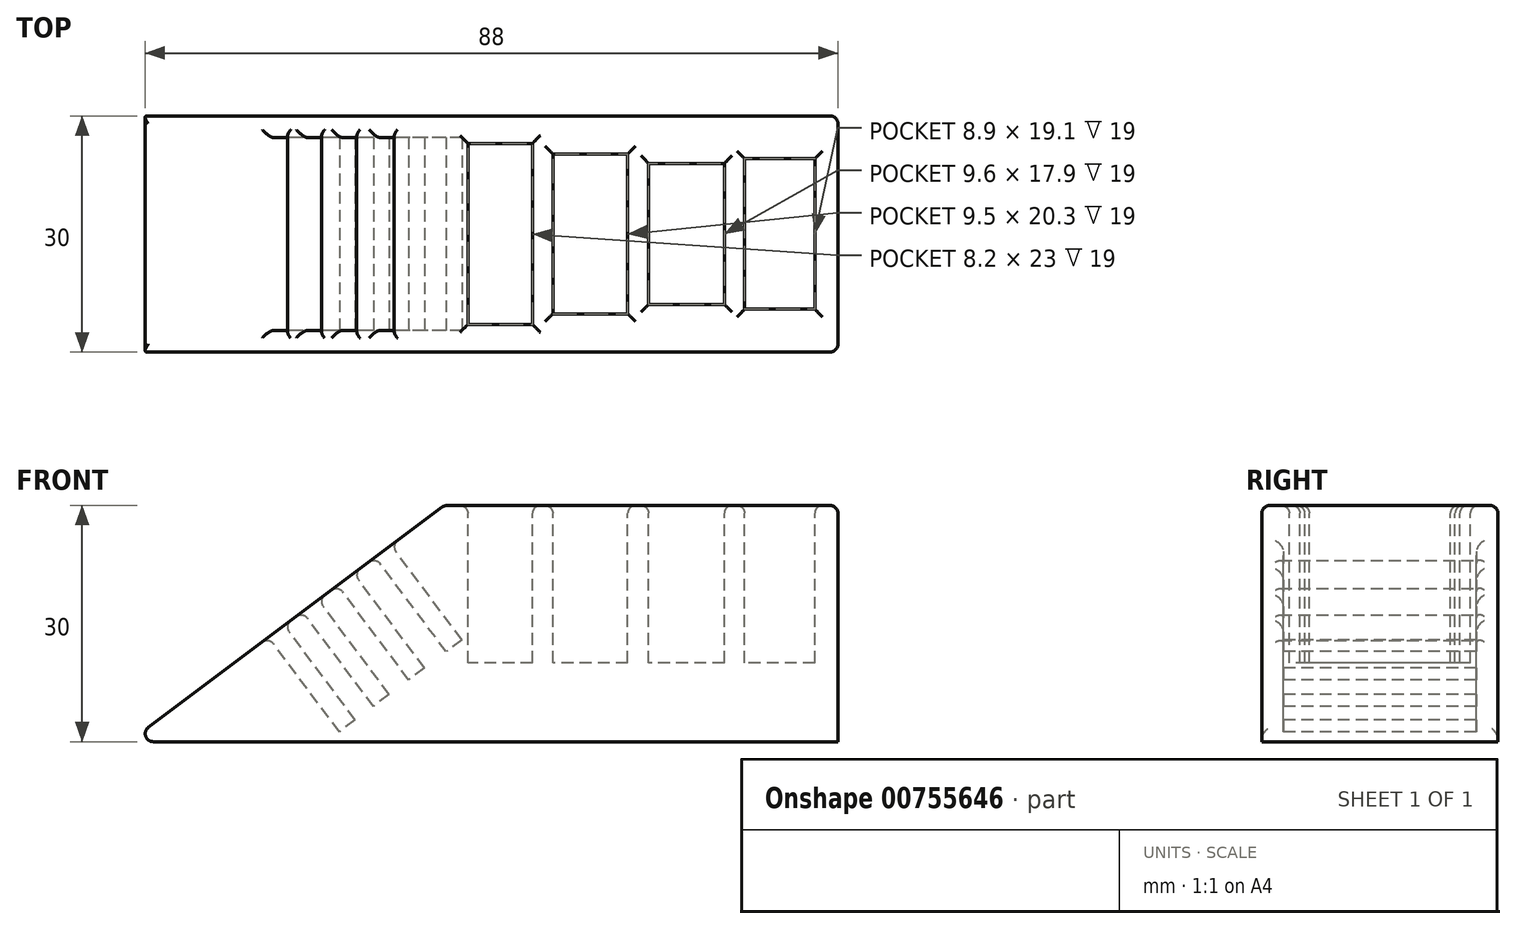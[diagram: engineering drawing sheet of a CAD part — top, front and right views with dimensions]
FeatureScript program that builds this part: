
annotation { "Feature Type Name" : "Feature", "Feature Type Description" : "" }
export const myFeature = defineFeature(function(context is Context, id is Id, definition is map)
    precondition{}
    {
        {
            var Q0;
            Q0=qCreatedBy(makeId("Front.planeOp"),FACE);
            var sketch = newSketch(context, id + "F0", { "sketchPlane" : qUnion([Q0])});
            skLineSegment(sketch, "E0.bottom", {"start": v(25, 15) * mm, "end": v(-25, 15) * mm});
            skLineSegment(sketch, "E0.top", {"start": v(25, -15) * mm, "end": v(-25, -15) * mm});
            skLineSegment(sketch, "E0.left", {"start": v(25, 15) * mm, "end": v(25, -15) * mm});
            skPoint(sketch, "E0.middle", {"position": v(0, 0) * mm});
            skLineSegment(sketch, "E1", {"start": v(-25, -15) * mm, "end": v(-65, -15) * mm});
            skLineSegment(sketch, "E2", {"start": v(-65, -15) * mm, "end": v(-25, 15) * mm});
            skSolve(sketch);
        }
        {
            var Q0;
            Q0=makeQuery(id+"F0.imprint","IMPRINT",FACE,{"disambiguationData":[TD([[makeQuery(id+"F0.imprint","IMPRINT",EDGE,{"derivedFrom":sQuery(id+"F0.wireOp",EDGE,"uxKhVTIh-jnt8-zA57-FXLV-tt7Bemn0Hdy7")}),-1.0]])]});
            var Q1;
            Q1=makeQuery(id+"F0.imprint","IMPRINT",FACE,{"disambiguationData":[TD([[makeQuery(id+"F0.imprint","IMPRINT",EDGE,{"derivedFrom":sQuery(id+"F0.wireOp",EDGE,"E0.bottom")}),1.0]])]});
            extrude(context, id + "F1", {"entities" : qUnion([Q0, Q1]), "endBound" : BoundingType.SYMMETRIC, "depth" : 30 * mm, "offsetDistance" : 25 * mm});
        }
        {
            var Q0;
            Q0=qCreatedBy(makeId("Top.planeOp"),FACE);
            cPlane(context, id + "F2", {"entities" : qUnion([Q0]), "cplaneType" : CPlaneType.OFFSET, "offset" : 20 * mm, "width" : 150 * mm, "height" : 150 * mm});
        }
        {
            var Q0;
            Q0=qCreatedBy(id+"F2.planeOp",FACE);
            var sketch = newSketch(context, id + "F3", { "sketchPlane" : qUnion([Q0])});
            skLineSegment(sketch, "E3.bottom", {"start": v(-13.8, 11.5) * mm, "end": v(-22, 11.5) * mm});
            skLineSegment(sketch, "E3.top", {"start": v(-13.8, -11.5) * mm, "end": v(-22, -11.5) * mm});
            skLineSegment(sketch, "E3.left", {"start": v(-13.8, 11.5) * mm, "end": v(-13.8, -11.5) * mm});
            skLineSegment(sketch, "E3.right", {"start": v(-22, 11.5) * mm, "end": v(-22, -11.5) * mm});
            skPoint(sketch, "E3.middle", {"position": v(-17.9, 0) * mm});
            skLineSegment(sketch, "E4.bottom", {"start": v(-1.7, 10.15) * mm, "end": v(-11.2, 10.15) * mm});
            skLineSegment(sketch, "E4.top", {"start": v(-1.7, -10.15) * mm, "end": v(-11.2, -10.15) * mm});
            skLineSegment(sketch, "E4.left", {"start": v(-1.7, 10.15) * mm, "end": v(-1.7, -10.15) * mm});
            skLineSegment(sketch, "E4.right", {"start": v(-11.2, 10.15) * mm, "end": v(-11.2, -10.15) * mm});
            skPoint(sketch, "E4.middle", {"position": v(-6.46, 0) * mm});
            skLineSegment(sketch, "E5.bottom", {"start": v(10.56, 8.95) * mm, "end": v(0.96, 8.95) * mm});
            skLineSegment(sketch, "E5.top", {"start": v(10.56, -8.95) * mm, "end": v(0.96, -8.95) * mm});
            skLineSegment(sketch, "E5.left", {"start": v(10.56, 8.95) * mm, "end": v(10.56, -8.95) * mm});
            skLineSegment(sketch, "E5.right", {"start": v(0.96, 8.95) * mm, "end": v(0.96, -8.95) * mm});
            skPoint(sketch, "E5.middle", {"position": v(5.76, 0) * mm});
            skLineSegment(sketch, "E6.bottom", {"start": v(22.06, 9.55) * mm, "end": v(13.16, 9.55) * mm});
            skLineSegment(sketch, "E6.top", {"start": v(22.06, -9.55) * mm, "end": v(13.16, -9.55) * mm});
            skLineSegment(sketch, "E6.left", {"start": v(22.06, 9.55) * mm, "end": v(22.06, -9.55) * mm});
            skLineSegment(sketch, "E6.right", {"start": v(13.16, 9.55) * mm, "end": v(13.16, -9.55) * mm});
            skPoint(sketch, "E6.middle", {"position": v(17.6, 0) * mm});
            skPoint(sketch, "E7.middle", {"position": v(-31.98, 0) * mm});
            skSolve(sketch);
        }
        {
            var Q0;
            Q0=makeQuery(id+"F3.imprint","IMPRINT",FACE,{"disambiguationData":[TD([[makeQuery(id+"F3.imprint","IMPRINT",EDGE,{"derivedFrom":sQuery(id+"F3.wireOp",EDGE,"E3.bottom")}),1.0]])]});
            var Q1;
            Q1=makeQuery(id+"F3.imprint","IMPRINT",FACE,{"disambiguationData":[TD([[makeQuery(id+"F3.imprint","IMPRINT",EDGE,{"derivedFrom":sQuery(id+"F3.wireOp",EDGE,"E4.bottom")}),1.0]])]});
            var Q2;
            Q2=makeQuery(id+"F3.imprint","IMPRINT",FACE,{"disambiguationData":[TD([[makeQuery(id+"F3.imprint","IMPRINT",EDGE,{"derivedFrom":sQuery(id+"F3.wireOp",EDGE,"E5.bottom")}),1.0]])]});
            var Q3;
            Q3=makeQuery(id+"F3.imprint","IMPRINT",FACE,{"disambiguationData":[TD([[makeQuery(id+"F3.imprint","IMPRINT",EDGE,{"derivedFrom":sQuery(id+"F3.wireOp",EDGE,"E6.bottom")}),1.0]])]});
            extrude(context, id + "F4", {"entities" : qUnion([Q0, Q1, Q2, Q3]), "operationType" : NewBodyOperationType.REMOVE, "oppositeDirection" : true, "depth" : 25 * mm, "offsetDistance" : 25 * mm});
        }
        {
            var Q0;
            Q0=makeQuery(id+"F1.opExtrude","SWEPT_FACE",FACE,{"disambiguationData":[OSD([sQuery(id+"F0.wireOp",EDGE,"E2")])]});
            var sketch = newSketch(context, id + "F5", { "sketchPlane" : qUnion([Q0])});
            skLineSegment(sketch, "E8.bottom", {"start": v(-19.44, 12.25) * mm, "end": v(-21.94, 12.25) * mm});
            skLineSegment(sketch, "E8.top", {"start": v(-19.44, -12.25) * mm, "end": v(-21.94, -12.25) * mm});
            skLineSegment(sketch, "E8.left", {"start": v(-19.44, 12.25) * mm, "end": v(-19.44, -12.25) * mm});
            skLineSegment(sketch, "E8.right", {"start": v(-21.94, 12.25) * mm, "end": v(-21.94, -12.25) * mm});
            skPoint(sketch, "E8.middle", {"position": v(-20.7, 0) * mm});
            skLineSegment(sketch, "E9.bottom", {"start": v(-25.4, 12.25) * mm, "end": v(-27.9, 12.25) * mm});
            skLineSegment(sketch, "E9.top", {"start": v(-25.4, -12.25) * mm, "end": v(-27.9, -12.25) * mm});
            skLineSegment(sketch, "E9.left", {"start": v(-25.4, 12.25) * mm, "end": v(-25.4, -12.25) * mm});
            skLineSegment(sketch, "E9.right", {"start": v(-27.9, 12.25) * mm, "end": v(-27.9, -12.25) * mm});
            skLineSegment(sketch, "E10.bottom", {"start": v(-31, 12.25) * mm, "end": v(-33.5, 12.25) * mm});
            skLineSegment(sketch, "E10.top", {"start": v(-31, -12.25) * mm, "end": v(-33.5, -12.25) * mm});
            skLineSegment(sketch, "E10.left", {"start": v(-31, 12.25) * mm, "end": v(-31, -12.25) * mm});
            skLineSegment(sketch, "E10.right", {"start": v(-33.5, 12.25) * mm, "end": v(-33.5, -12.25) * mm});
            skLineSegment(sketch, "E11.bottom", {"start": v(-36.4, 12.25) * mm, "end": v(-38.9, 12.25) * mm});
            skLineSegment(sketch, "E11.top", {"start": v(-36.4, -12.25) * mm, "end": v(-38.9, -12.25) * mm});
            skLineSegment(sketch, "E11.left", {"start": v(-36.4, 12.25) * mm, "end": v(-36.4, -12.25) * mm});
            skLineSegment(sketch, "E11.right", {"start": v(-38.9, 12.25) * mm, "end": v(-38.9, -12.25) * mm});
            skSolve(sketch);
        }
        {
            var Q0;
            Q0=makeQuery(id+"F5.imprint","IMPRINT",FACE,{"disambiguationData":[TD([[makeQuery(id+"F5.imprint","IMPRINT",EDGE,{"derivedFrom":sQuery(id+"F5.wireOp",EDGE,"E8.bottom")}),1.0]])]});
            extrude(context, id + "F6", {"entities" : qUnion([Q0]), "operationType" : NewBodyOperationType.REMOVE, "oppositeDirection" : true, "depth" : 15 * mm, "offsetDistance" : 25 * mm});
        }
        {
            var Q0;
            Q0=makeQuery(id+"F5.imprint","IMPRINT",FACE,{"disambiguationData":[TD([[makeQuery(id+"F5.imprint","IMPRINT",EDGE,{"derivedFrom":sQuery(id+"F5.wireOp",EDGE,"E9.bottom")}),1.0]])]});
            var Q1;
            Q1=makeQuery(id+"F5.imprint","IMPRINT",FACE,{"disambiguationData":[TD([[makeQuery(id+"F5.imprint","IMPRINT",EDGE,{"derivedFrom":sQuery(id+"F5.wireOp",EDGE,"E10.bottom")}),1.0]])]});
            var Q2;
            Q2=makeQuery(id+"F5.imprint","IMPRINT",FACE,{"disambiguationData":[TD([[makeQuery(id+"F5.imprint","IMPRINT",EDGE,{"derivedFrom":sQuery(id+"F5.wireOp",EDGE,"E11.bottom")}),1.0]])]});
            extrude(context, id + "F7", {"entities" : qUnion([Q0, Q1, Q2]), "operationType" : NewBodyOperationType.REMOVE, "oppositeDirection" : true, "depth" : 15 * mm, "offsetDistance" : 25 * mm});
        }
        {
            var Q0;
            Q0=makeQuery(id+"F1.opExtrude","SWEPT_FACE",FACE,{"disambiguationData":[OSD([sQuery(id+"F0.wireOp",EDGE,"E2")])]});
            var Q1;
            Q1=makeQuery(id+"F1.opExtrude","SWEPT_FACE",FACE,{"disambiguationData":[OSD([sQuery(id+"F0.wireOp",EDGE,"E0.bottom")])]});
            var Q2;
            Q2=makeQuery(id+"F1.opExtrude","CAP_EDGE",EDGE,{"disambiguationData":[OSD([sQuery(id+"F0.wireOp",EDGE,"E0.bottom")])],"isStart":false});
            var Q3;
            Q3=makeQuery(id+"F1.opExtrude","SWEPT_EDGE",EDGE,{"disambiguationData":[OSD([sQuery(id+"F0.wireOp",EDGE,"E0.bottom"),sQuery(id+"F0.wireOp",EDGE,"E0.left")])]});
            var Q4;
            Q4=makeQuery(id+"F1.opExtrude","CAP_EDGE",EDGE,{"disambiguationData":[OSD([sQuery(id+"F0.wireOp",EDGE,"E0.left")])],"isStart":false});
            var Q5;
            Q5=makeQuery(id+"F1.opExtrude","CAP_EDGE",EDGE,{"disambiguationData":[OSD([sQuery(id+"F0.wireOp",EDGE,"E0.left")])],"isStart":true});
            fillet(context, id + "F8", {"entities" : qUnion([Q0, Q1, Q2, Q3, Q4, Q5]), "radius" : 1 * mm, "tangentPropagation" : true, "allowEdgeOverflow" : false});
        }
    });
